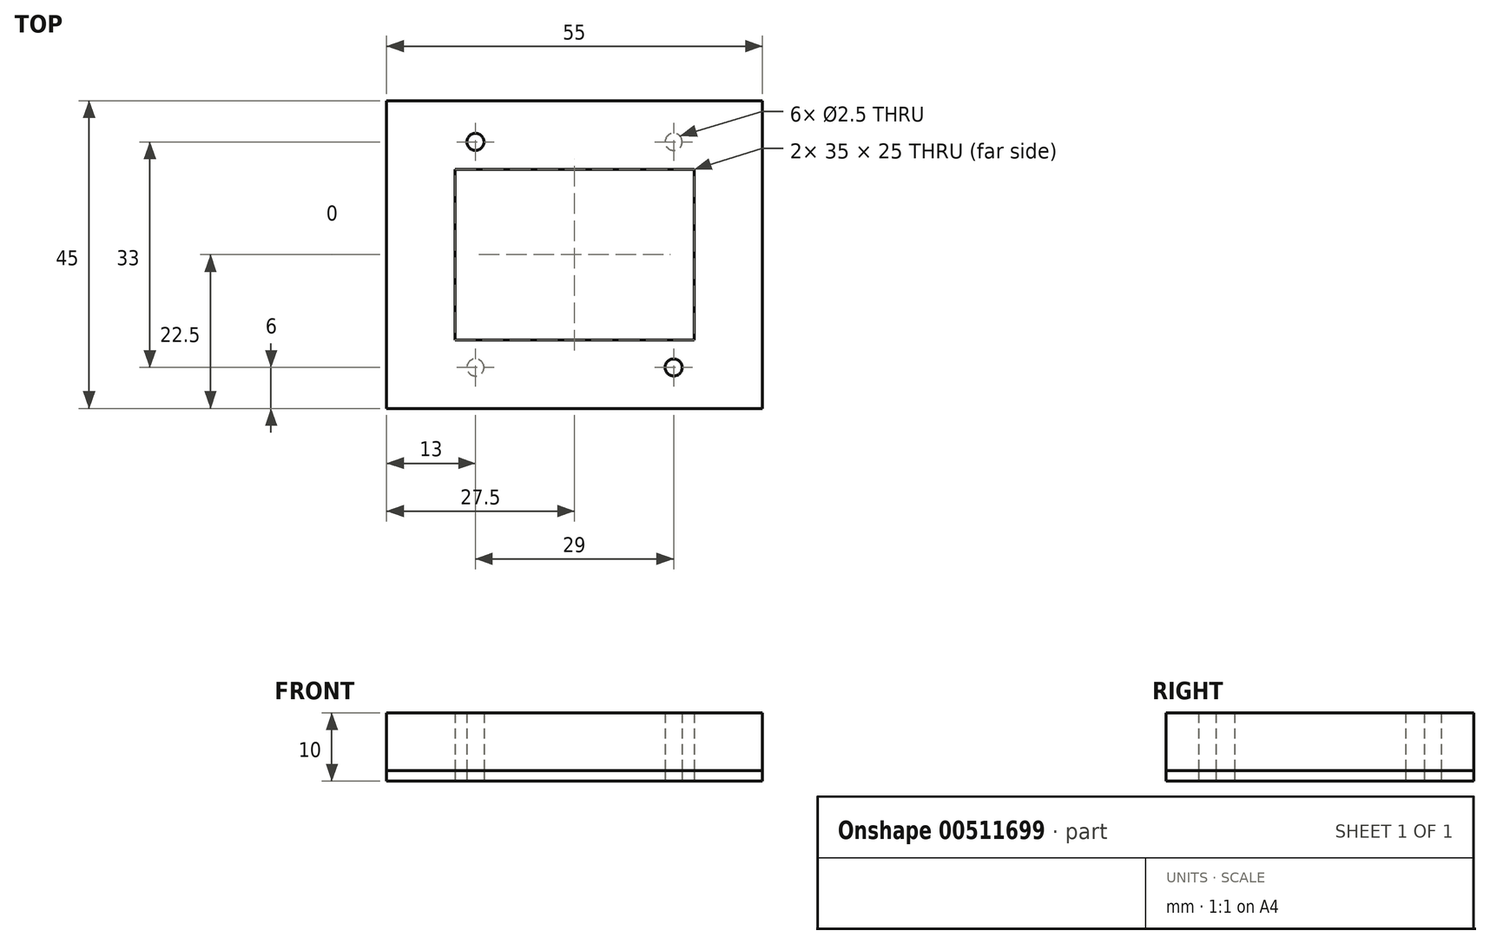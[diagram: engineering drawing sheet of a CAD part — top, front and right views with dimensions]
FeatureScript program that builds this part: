
annotation { "Feature Type Name" : "Feature", "Feature Type Description" : "" }
export const myFeature = defineFeature(function(context is Context, id is Id, definition is map)
    precondition{}
    {
        {
            var Q0;
            Q0=qCreatedBy(makeId("Top.planeOp"),FACE);
            var sketch = newSketch(context, id + "F0", { "sketchPlane" : qUnion([Q0])});
            skLineSegment(sketch, "E0.bottom", {"start": v(27.5, -22.5) * mm, "end": v(-27.5, -22.5) * mm});
            skLineSegment(sketch, "E0.top", {"start": v(27.5, 22.5) * mm, "end": v(-27.5, 22.5) * mm});
            skLineSegment(sketch, "E0.left", {"start": v(27.5, -22.5) * mm, "end": v(27.5, 22.5) * mm});
            skLineSegment(sketch, "E0.right", {"start": v(-27.5, -22.5) * mm, "end": v(-27.5, 22.5) * mm});
            skPoint(sketch, "E0.middle", {"position": v(0, 0) * mm});
            skLineSegment(sketch, "E1.bottom", {"start": v(17.5, -12.5) * mm, "end": v(-17.5, -12.5) * mm});
            skLineSegment(sketch, "E1.top", {"start": v(17.5, 12.5) * mm, "end": v(-17.5, 12.5) * mm});
            skLineSegment(sketch, "E1.left", {"start": v(17.5, -12.5) * mm, "end": v(17.5, 12.5) * mm});
            skLineSegment(sketch, "E1.right", {"start": v(-17.5, -12.5) * mm, "end": v(-17.5, 12.5) * mm});
            skCircle(sketch, "E2", {"center": v(-14.5, -16.5) * mm, "radius": 1.25 * mm});
            skCircle(sketch, "E3.MirrorC", {"center": v(-14.5, 16.5) * mm, "radius": 1.25 * mm});
            skCircle(sketch, "E4.MirrorC", {"center": v(14.5, 16.5) * mm, "radius": 1.25 * mm});
            skCircle(sketch, "E5.MirrorC", {"center": v(14.5, -16.5) * mm, "radius": 1.25 * mm});
            skSolve(sketch);
        }
        {
            var Q0;
            Q0=makeQuery(id+"F0.imprint","IMPRINT",FACE,{"disambiguationData":[TD([[makeQuery(id+"F0.imprint","IMPRINT",EDGE,{"derivedFrom":sQuery(id+"F0.wireOp",EDGE,"E3.MirrorC")}),-1.0]])]});
            var Q1;
            Q1=makeQuery(id+"F0.imprint","IMPRINT",FACE,{"disambiguationData":[TD([[makeQuery(id+"F0.imprint","IMPRINT",EDGE,{"derivedFrom":sQuery(id+"F0.wireOp",EDGE,"E2")}),1.0]])]});
            var Q2;
            Q2=makeQuery(id+"F0.imprint","IMPRINT",FACE,{"disambiguationData":[TD([[makeQuery(id+"F0.imprint","IMPRINT",EDGE,{"derivedFrom":sQuery(id+"F0.wireOp",EDGE,"E5.MirrorC")}),-1.0]])]});
            var Q3;
            Q3=makeQuery(id+"F0.imprint","IMPRINT",FACE,{"disambiguationData":[TD([[makeQuery(id+"F0.imprint","IMPRINT",EDGE,{"derivedFrom":sQuery(id+"F0.wireOp",EDGE,"E4.MirrorC")}),1.0]])]});
            var Q4;
            Q4=sQuery(id+"F0.wireOp",EDGE,"E3.MirrorC");
            var Q5;
            Q5=sQuery(id+"F0.wireOp",EDGE,"E4.MirrorC");
            var Q6;
            Q6=sQuery(id+"F0.wireOp",EDGE,"E5.MirrorC");
            var Q7;
            Q7=sQuery(id+"F0.wireOp",EDGE,"E2");
            extrude(context, id + "F1", {"entities" : qUnion([Q0, Q1, Q2, Q3]), "surfaceEntities" : qUnion([Q4, Q5, Q6, Q7]), "depth" : 10 * mm, "offsetDistance" : 25 * mm});
        }
        {
            var Q0;
            Q0=makeQuery(id+"F0.imprint","IMPRINT",FACE,{"disambiguationData":[TD([[makeQuery(id+"F0.imprint","IMPRINT",EDGE,{"derivedFrom":sQuery(id+"F0.wireOp",EDGE,"E0.bottom")}),-1.0]])]});
            extrude(context, id + "F2", {"entities" : qUnion([Q0]), "depth" : 1.5 * mm, "offsetDistance" : 25 * mm});
        }
    });
